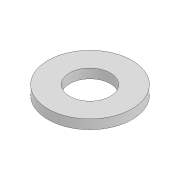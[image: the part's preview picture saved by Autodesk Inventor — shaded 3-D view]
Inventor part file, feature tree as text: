
AUTODESK INVENTOR PART (.ipt)
format: ipt  version: 2022 (Build 260153000, 153)  size: 81,408 bytes
history: native  units: mm
features: extrude x1, sketch x1
ambient origin geometry x8: Origin, YZ Plane, XZ Plane, XY Plane, X Axis, Y Axis, Z Axis, Center Point
bodies: Solid1 (feature_tree)
feature tree (2):
  extrude  "Extrusion1"  Depth=1.0mm
  sketch  "Sketch1"  dims[d0=4.35mm d1=9.0mm d2=1.0mm d3=0.0mm]
